FCSTD DOCUMENT  (FreeCAD 0.20R29410 (Git))
Label: grip2
License: All rights reserved
LicenseURL: http://en.wikipedia.org/wiki/All_rights_reserved
objects: Sketcher::SketchObject×1
note: 1 computed .brp shape members not serialized (recipe doc carries the construction recipe); baked Part::Feature solids carry a one-line shape summary decoded from their .brp

FEATURE [Sketcher::SketchObject] Sketch
  FullyConstrained = false
  sketch-geometry (21):
    g0: LineSegment StartX=0 StartY=0 StartZ=0 EndX=2.5 EndY=0 EndZ=0
    g1: LineSegment StartX=38.6817 StartY=17.0554 StartZ=0 EndX=2.5 EndY=0 EndZ=0
    g2: LineSegment StartX=0 StartY=0 StartZ=0 EndX=-2.5 EndY=0 EndZ=0
    g3: LineSegment StartX=-2.5 StartY=0 StartZ=0 EndX=-38.6817 EndY=17.0554 EndZ=0
    g4: LineSegment StartX=2.5 StartY=0 StartZ=0 EndX=10 EndY=-12.9904 EndZ=0
    g5: LineSegment StartX=38.6817 StartY=17.0554 StartZ=0 EndX=46.1817 EndY=4.06506 EndZ=0
    g6: LineSegment StartX=46.1817 StartY=4.06506 StartZ=0 EndX=10 EndY=-12.9904 EndZ=0
    g7: LineSegment StartX=-2.5 StartY=0 StartZ=0 EndX=-10 EndY=-12.9904 EndZ=0
    g8: LineSegment StartX=-10 StartY=-12.9904 StartZ=0 EndX=10 EndY=-12.9904 EndZ=0
    g9: LineSegment StartX=38.6817 StartY=17.0554 StartZ=0 EndX=38.6817 EndY=37.0554 EndZ=0
    g10: LineSegment StartX=46.1817 StartY=34.0651 StartZ=0 EndX=46.1817 EndY=4.06506 EndZ=0
    g11: LineSegment StartX=-38.6817 StartY=17.0554 StartZ=0 EndX=-38.6817 EndY=37.0554 EndZ=0
    g12: LineSegment StartX=-46.1817 StartY=34.0651 StartZ=0 EndX=-46.1817 EndY=4.06506 EndZ=0
    g13: LineSegment StartX=-46.1817 StartY=4.06506 StartZ=0 EndX=-38.6817 EndY=17.0554 EndZ=0
    g14: LineSegment StartX=-46.1817 StartY=4.06506 StartZ=0 EndX=-10 EndY=-12.9904 EndZ=0
    g15: LineSegment StartX=38.6817 StartY=37.0554 StartZ=0 EndX=36.5619 EndY=42.1402 EndZ=0
    g16: LineSegment StartX=36.5619 StartY=42.1402 StartZ=0 EndX=36.5619 EndY=57.1402 EndZ=0
    g17: LineSegment StartX=36.5619 StartY=57.1402 StartZ=0 EndX=46.1817 EndY=34.0651 EndZ=0
    g18: LineSegment StartX=-38.6817 StartY=37.0554 StartZ=0 EndX=-36.5619 EndY=42.1402 EndZ=0
    g19: LineSegment StartX=-36.5619 StartY=42.1402 StartZ=0 EndX=-36.5619 EndY=57.1402 EndZ=0
    g20: LineSegment StartX=-36.5619 StartY=57.1402 StartZ=0 EndX=-46.1817 EndY=34.0651 EndZ=0
  constraints (57):
    c: Coincident(g0,g-1)
    c: PointOnObject(g0,g-1)
    c: Coincident(g1,g0)
    c: Coincident(g2,g0)
    c: PointOnObject(g2,g-1)
    c: Coincident(g3,g2)
    c: Equal(g2,g0)
    c: Equal(g3,g1)
    c: DistanceX(g2,g2) = 2.5
    c: Coincident(g4,g0)
    c: Coincident(g5,g1)
    c: Coincident(g6,g5)
    c: Coincident(g6,g4)
    c: Angle(g0,g4) = 2.0944
    c: Parallel(g4,g5)
    c: Parallel(g1,g6)
    c: Coincident(g7,g2)
    c: Coincident(g8,g4)
    c: Horizontal(g8)
    c: Coincident(g8,g7)
    c: Equal(g7,g4)
    c: Coincident(g9,g1)
    c: Coincident(g10,g5)
    c: Vertical(g9)
    c: Vertical(g10)
    c: Coincident(g11,g3)
    c: Vertical(g11)
    c: Vertical(g12)
    c: Coincident(g13,g12)
    c: Coincident(g13,g3)
    c: Coincident(g14,g12)
    c: Coincident(g14,g7)
    c: Equal(g11,g9)
    c: Equal(g10,g12)
    c: Equal(g13,g5)
    c: Distance(g10) = 30
    c: Distance(g6) = 40
    c: Distance(g9) = 20
    c: Equal(g14,g6)
    c: Coincident(g15,g9)
    c: Coincident(g17,g10)
    c: Coincident(g15,g16)
    c: Coincident(g17,g16)
    c: Vertical(g16)
    c: Parallel(g15,g17)
    c: Distance(g17) = 25
    c: Distance(g16) = 15
    c: Coincident(g18,g11)
    c: Vertical(g19)
    c: Coincident(g20,g12)
    c: Coincident(g19,g20)
    c: Coincident(g19,g18)
    c: Equal(g17,g20)
    c: Equal(g18,g15)
    c: Equal(g16,g19)
    c: Horizontal(g19,g16)
    c: Distance(g7) = 15
